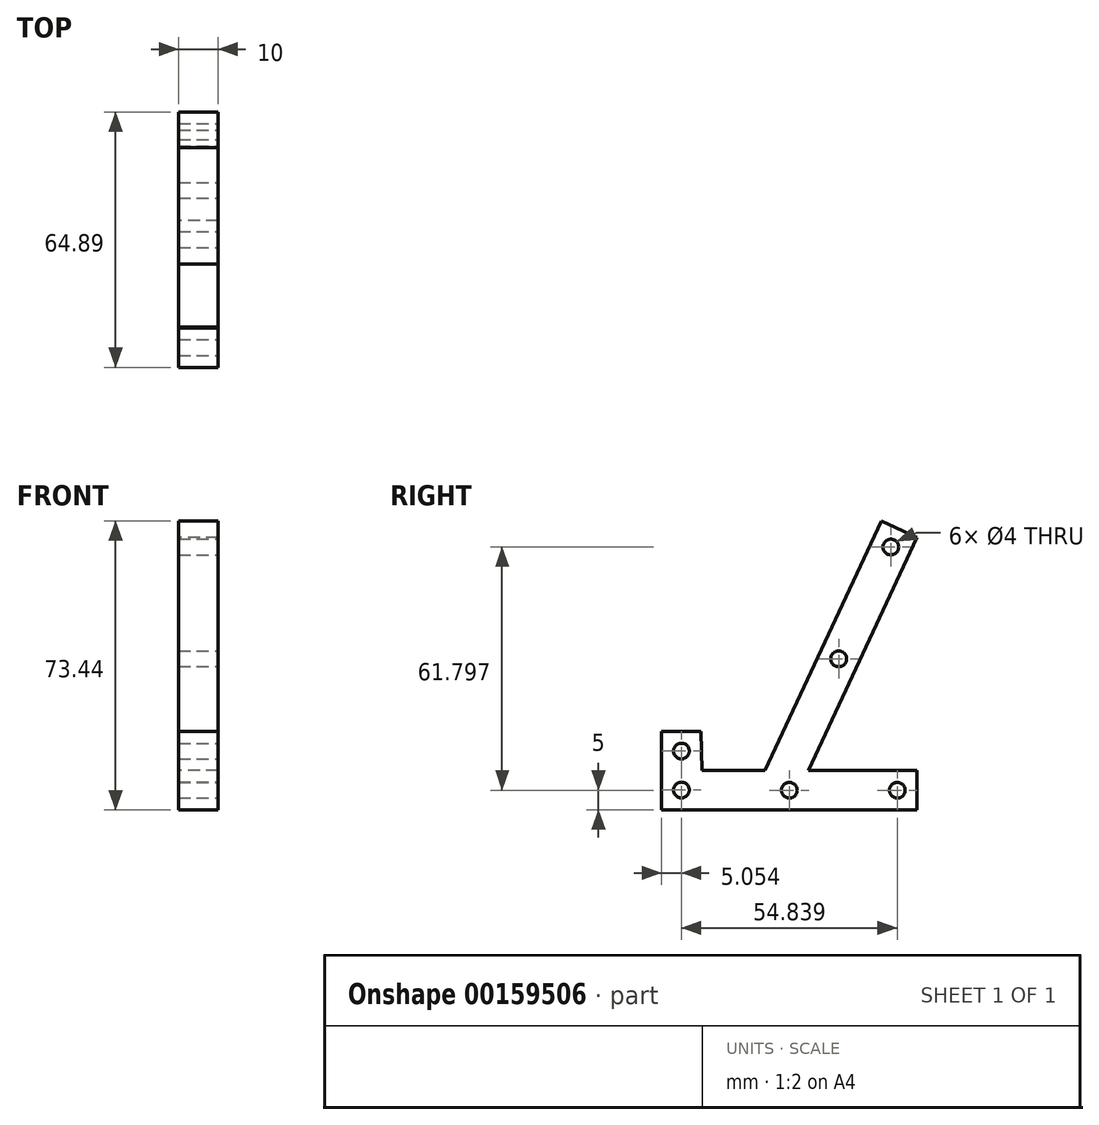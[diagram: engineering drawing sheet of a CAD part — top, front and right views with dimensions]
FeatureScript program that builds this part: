
annotation { "Feature Type Name" : "Feature", "Feature Type Description" : "" }
export const myFeature = defineFeature(function(context is Context, id is Id, definition is map)
    precondition{}
    {
        {
            var Q0;
            Q0=qCreatedBy(makeId("Right.planeOp"),FACE);
            var sketch = newSketch(context, id + "F0", { "sketchPlane" : qUnion([Q0])});
            skLineSegment(sketch, "E0.bottom", {"start": v(23, 5) * mm, "end": v(-4.62, 5) * mm});
            skLineSegment(sketch, "E0.top", {"start": v(23, -5) * mm, "end": v(-41.9, -5) * mm});
            skPoint(sketch, "E0.middle", {"position": v(0, 0) * mm});
            skLineSegment(sketch, "E1.bottom", {"start": v(23, 64.22) * mm, "end": v(13.93, 68.44) * mm});
            skLineSegment(sketch, "E1.left", {"start": v(23, 64.22) * mm, "end": v(-4.62, 5) * mm});
            skLineSegment(sketch, "E1.right", {"start": v(13.93, 68.44) * mm, "end": v(-15.65, 5) * mm});
            skPoint(sketch, "E1.middle", {"position": v(3.67, 34.6) * mm});
            skLineSegment(sketch, "E2", {"start": v(23, 5) * mm, "end": v(23, -5) * mm});
            skLineSegment(sketch, "E3.top", {"start": v(-41.9, 15) * mm, "end": v(-31.9, 15) * mm});
            skLineSegment(sketch, "E3.right", {"start": v(-31.7, 5) * mm, "end": v(-31.9, 15) * mm});
            skLineSegment(sketch, "E4", {"start": v(-31.7, 5) * mm, "end": v(-15.65, 5) * mm});
            skLineSegment(sketch, "E5", {"start": v(-41.9, 15) * mm, "end": v(-41.9, -5) * mm});
            skSolve(sketch);
        }
        {
            var Q0;
            Q0=makeQuery(id+"F0.imprint","IMPRINT",FACE,{"disambiguationData":[TD([[makeQuery(id+"F0.imprint","IMPRINT",EDGE,{"derivedFrom":sQuery(id+"F0.wireOp",EDGE,"E0.bottom")}),1.0]])]});
            extrude(context, id + "F1", {"entities" : qUnion([Q0]), "depth" : 10 * mm});
        }
        {
            var Q0;
            Q0=makeQuery(id+"F1.opExtrude","CAP_FACE",FACE,{"disambiguationData":[OSD([sQuery(id+"F0.wireOp",EDGE,"E0.bottom"),sQuery(id+"F0.wireOp",EDGE,"E0.top"),sQuery(id+"F0.wireOp",EDGE,"E1.bottom"),sQuery(id+"F0.wireOp",EDGE,"E1.left"),sQuery(id+"F0.wireOp",EDGE,"E1.right"),sQuery(id+"F0.wireOp",EDGE,"E2"),sQuery(id+"F0.wireOp",EDGE,"E3.top"),sQuery(id+"F0.wireOp",EDGE,"E3.right"),sQuery(id+"F0.wireOp",EDGE,"E4"),sQuery(id+"F0.wireOp",EDGE,"E5")])],"isStart":false});
            var sketch = newSketch(context, id + "F2", { "sketchPlane" : qUnion([Q0])});
            skLineSegment(sketch, "E6", {"start": v(18.46, 66.33) * mm, "end": v(16.35, 61.8) * mm, "construction": true});
            skLineSegment(sketch, "E7", {"start": v(16.35, 61.8) * mm, "end": v(11.82, 63.91) * mm, "construction": true});
            skLineSegment(sketch, "E8", {"start": v(16.35, 61.8) * mm, "end": v(20.88, 59.68) * mm, "construction": true});
            skPoint(sketch, "E9.startSnap0", {"position": v(-36.9, 15) * mm});
            skLineSegment(sketch, "E10", {"start": v(-36.85, 9.95) * mm, "end": v(-36.9, 15) * mm, "construction": true});
            skLineSegment(sketch, "E11", {"start": v(-36.85, 9.95) * mm, "end": v(-31.8, 10) * mm, "construction": true});
            skLineSegment(sketch, "E12", {"start": v(-36.85, 9.95) * mm, "end": v(-41.9, 9.9) * mm, "construction": true});
            skLineSegment(sketch, "E13", {"start": v(-36.85, 0.05) * mm, "end": v(-36.85, -5) * mm, "construction": true});
            skLineSegment(sketch, "E14", {"start": v(-36.85, 0.05) * mm, "end": v(-41.9, 0.05) * mm, "construction": true});
            skLineSegment(sketch, "E15", {"start": v(18, 0) * mm, "end": v(23, 0) * mm, "construction": true});
            skLineSegment(sketch, "E16", {"start": v(18, 0) * mm, "end": v(18, 5) * mm, "construction": true});
            skLineSegment(sketch, "E17", {"start": v(18, 0) * mm, "end": v(18, -5) * mm, "construction": true});
            skLineSegment(sketch, "E18", {"start": v(-9.43, 0) * mm, "end": v(-9.43, -5) * mm, "construction": true});
            skLineSegment(sketch, "E19", {"start": v(-9.43, 0) * mm, "end": v(18, 0) * mm, "construction": true});
            skLineSegment(sketch, "E20", {"start": v(-9.43, 0) * mm, "end": v(-36.85, 0.05) * mm, "construction": true});
            skLineSegment(sketch, "E21", {"start": v(3.1, 33.4) * mm, "end": v(7.64, 31.29) * mm, "construction": true});
            skLineSegment(sketch, "E22", {"start": v(3.1, 33.4) * mm, "end": v(-1.43, 35.51) * mm, "construction": true});
            skLineSegment(sketch, "E23", {"start": v(-10.14, 5) * mm, "end": v(3.1, 33.4) * mm, "construction": true});
            skLineSegment(sketch, "E24", {"start": v(3.1, 33.4) * mm, "end": v(16.35, 61.8) * mm, "construction": true});
            skLineSegment(sketch, "E25", {"start": v(-15.65, 5) * mm, "end": v(-4.62, 5) * mm, "construction": true});
            skSolve(sketch);
        }
        {
            var Q0;
            Q0=sQuery(id+"F2.wireOp",VERTEX,"E8.start");
            var Q1;
            Q1=sQuery(id+"F2.wireOp",VERTEX,"E15.start");
            var Q2;
            Q2=sQuery(id+"F2.wireOp",VERTEX,"E20.start");
            var Q3;
            Q3=sQuery(id+"F2.wireOp",VERTEX,"E13.start");
            var Q4;
            Q4=sQuery(id+"F2.wireOp",VERTEX,"ygwfUP1r-Xf9U-DtoX-q1UJ-cSdGN7rKCHlz.center");
            var Q5;
            Q5=sQuery(id+"F2.wireOp",VERTEX,"E24.start");
            var Q6;
            Q6=sQuery(id+"F2.wireOp",VERTEX,"E10.start");
            var Q7;
            Q7=makeQuery(id+"F1.opExtrude","SWEPT_BODY",BODY,{"disambiguationData":[OSD([sQuery(id+"F0.wireOp",EDGE,"E0.bottom"),sQuery(id+"F0.wireOp",EDGE,"E0.top"),sQuery(id+"F0.wireOp",EDGE,"E1.bottom"),sQuery(id+"F0.wireOp",EDGE,"E1.left"),sQuery(id+"F0.wireOp",EDGE,"E1.right"),sQuery(id+"F0.wireOp",EDGE,"E2"),sQuery(id+"F0.wireOp",EDGE,"E3.top"),sQuery(id+"F0.wireOp",EDGE,"E3.right"),sQuery(id+"F0.wireOp",EDGE,"E4"),sQuery(id+"F0.wireOp",EDGE,"E5")])]});
            hole(context, id + "F3", {"style" : HoleStyle.SIMPLE, "endStyle" : HoleEndStyle.BLIND, "holeDiameter" : 4 * mm, "holeDepth" : 12 * mm, "locations" : qUnion([Q0, Q1, Q2, Q3, Q4, Q5, Q6]), "scope" : qUnion([Q7])});
        }
    });
